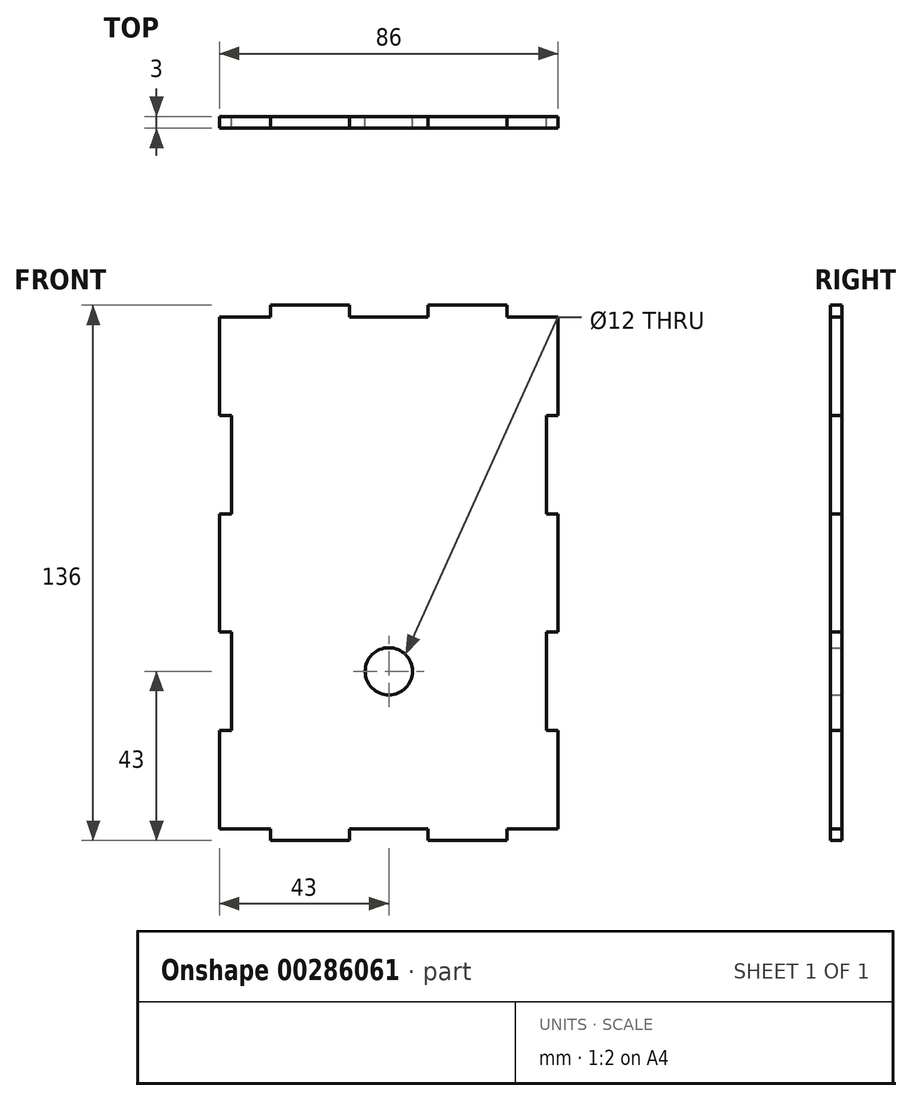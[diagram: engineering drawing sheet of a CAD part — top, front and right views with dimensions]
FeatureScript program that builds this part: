
annotation { "Feature Type Name" : "Feature", "Feature Type Description" : "" }
export const myFeature = defineFeature(function(context is Context, id is Id, definition is map)
    precondition{}
    {
        {
            var Q0;
            Q0=qCreatedBy(makeId("Front.planeOp"),FACE);
            var sketch = newSketch(context, id + "F0", { "sketchPlane" : qUnion([Q0])});
            skLineSegment(sketch, "E0.bottom", {"start": v(40, -65) * mm, "end": v(-40, -65) * mm, "construction": true});
            skLineSegment(sketch, "E0.top", {"start": v(40, 65) * mm, "end": v(-40, 65) * mm, "construction": true});
            skLineSegment(sketch, "E0.left", {"start": v(40, -65) * mm, "end": v(40, 65) * mm, "construction": true});
            skLineSegment(sketch, "E0.right", {"start": v(-40, -65) * mm, "end": v(-40, 65) * mm, "construction": true});
            skPoint(sketch, "E0.middle", {"position": v(0, 0) * mm});
            skLineSegment(sketch, "E1", {"start": v(-40, 65) * mm, "end": v(-43, 65) * mm});
            skLineSegment(sketch, "E2", {"start": v(-43, 65) * mm, "end": v(-43, 40) * mm});
            skLineSegment(sketch, "E3", {"start": v(-43, 40) * mm, "end": v(-40, 40) * mm});
            skLineSegment(sketch, "E4", {"start": v(-40, 40) * mm, "end": v(-40, 15) * mm});
            skLineSegment(sketch, "E5", {"start": v(-40, 15) * mm, "end": v(-43, 15) * mm});
            skLineSegment(sketch, "E6", {"start": v(-43, 15) * mm, "end": v(-43, 0) * mm});
            skLineSegment(sketch, "E7", {"start": v(-40, 65) * mm, "end": v(-30, 65) * mm});
            skLineSegment(sketch, "E8", {"start": v(-30, 65) * mm, "end": v(-30, 68) * mm});
            skLineSegment(sketch, "E9", {"start": v(-30, 68) * mm, "end": v(-10, 68) * mm});
            skLineSegment(sketch, "E10", {"start": v(-10, 68) * mm, "end": v(-10, 65) * mm});
            skLineSegment(sketch, "E11", {"start": v(-10, 65) * mm, "end": v(0, 65) * mm});
            skLineSegment(sketch, "E12.MirrorCS", {"start": v(10, 68) * mm, "end": v(10, 65) * mm});
            skLineSegment(sketch, "E13.MirrorCS", {"start": v(30, 65) * mm, "end": v(30, 68) * mm});
            skLineSegment(sketch, "E14.MirrorCS", {"start": v(40, 15) * mm, "end": v(43, 15) * mm});
            skLineSegment(sketch, "E15.MirrorCS", {"start": v(43, 40) * mm, "end": v(40, 40) * mm});
            skLineSegment(sketch, "E16.MirrorCS", {"start": v(40, 65) * mm, "end": v(43, 65) * mm});
            skLineSegment(sketch, "E17.MirrorCS", {"start": v(30, 68) * mm, "end": v(10, 68) * mm});
            skLineSegment(sketch, "E18.MirrorCS", {"start": v(-40, 65) * mm, "end": v(40, 65) * mm, "construction": true});
            skLineSegment(sketch, "E19.MirrorCS", {"start": v(40, 65) * mm, "end": v(30, 65) * mm});
            skLineSegment(sketch, "E20.MirrorCS", {"start": v(10, 65) * mm, "end": v(0, 65) * mm});
            skLineSegment(sketch, "E21.MirrorCS", {"start": v(43, 15) * mm, "end": v(43, 0) * mm});
            skLineSegment(sketch, "E22.MirrorCS", {"start": v(43, 65) * mm, "end": v(43, 40) * mm});
            skLineSegment(sketch, "E23.MirrorCS", {"start": v(40, 40) * mm, "end": v(40, 15) * mm});
            skLineSegment(sketch, "E24.MirrorCS", {"start": v(30, -65) * mm, "end": v(30, -68) * mm});
            skLineSegment(sketch, "E25.MirrorCS", {"start": v(43, -40) * mm, "end": v(40, -40) * mm});
            skLineSegment(sketch, "E26.MirrorCS", {"start": v(-30, -65) * mm, "end": v(-30, -68) * mm});
            skLineSegment(sketch, "E27.MirrorCS", {"start": v(10, -68) * mm, "end": v(10, -65) * mm});
            skLineSegment(sketch, "E28.MirrorCS", {"start": v(-40, -65) * mm, "end": v(-43, -65) * mm});
            skLineSegment(sketch, "E29.MirrorCS", {"start": v(-43, -40) * mm, "end": v(-40, -40) * mm});
            skLineSegment(sketch, "E30.MirrorCS", {"start": v(40, -15) * mm, "end": v(43, -15) * mm});
            skLineSegment(sketch, "E31.MirrorCS", {"start": v(40, -65) * mm, "end": v(43, -65) * mm});
            skLineSegment(sketch, "E32.MirrorCS", {"start": v(-10, -68) * mm, "end": v(-10, -65) * mm});
            skLineSegment(sketch, "E33.MirrorCS", {"start": v(-40, -15) * mm, "end": v(-43, -15) * mm});
            skLineSegment(sketch, "E34.MirrorCS", {"start": v(40, 65) * mm, "end": v(40, -65) * mm, "construction": true});
            skLineSegment(sketch, "E35.MirrorCS", {"start": v(30, -68) * mm, "end": v(10, -68) * mm});
            skLineSegment(sketch, "E36.MirrorCS", {"start": v(-40, -65) * mm, "end": v(40, -65) * mm, "construction": true});
            skLineSegment(sketch, "E37.MirrorCS", {"start": v(40, -65) * mm, "end": v(30, -65) * mm});
            skLineSegment(sketch, "E38.MirrorCS", {"start": v(43, -15) * mm, "end": v(43, 0) * mm});
            skLineSegment(sketch, "E39.MirrorCS", {"start": v(40, -40) * mm, "end": v(40, -15) * mm});
            skLineSegment(sketch, "E40.MirrorCS", {"start": v(-30, -68) * mm, "end": v(-10, -68) * mm});
            skLineSegment(sketch, "E41.MirrorCS", {"start": v(-40, 65) * mm, "end": v(-40, -65) * mm, "construction": true});
            skLineSegment(sketch, "E42.MirrorCS", {"start": v(-10, -65) * mm, "end": v(0, -65) * mm});
            skLineSegment(sketch, "E43.MirrorCS", {"start": v(-43, -15) * mm, "end": v(-43, 0) * mm});
            skLineSegment(sketch, "E44.MirrorCS", {"start": v(-43, -65) * mm, "end": v(-43, -40) * mm});
            skLineSegment(sketch, "E45.MirrorCS", {"start": v(-40, -40) * mm, "end": v(-40, -15) * mm});
            skLineSegment(sketch, "E46.MirrorCS", {"start": v(-40, -65) * mm, "end": v(-30, -65) * mm});
            skLineSegment(sketch, "E47.MirrorCS", {"start": v(10, -65) * mm, "end": v(0, -65) * mm});
            skLineSegment(sketch, "E48.MirrorCS", {"start": v(43, -65) * mm, "end": v(43, -40) * mm});
            skCircle(sketch, "E49", {"center": v(0, -25) * mm, "radius": 6 * mm});
            skSolve(sketch);
        }
        {
            var Q0;
            Q0=makeQuery(id+"F0.imprint","IMPRINT",FACE,{"disambiguationData":[TD([[makeQuery(id+"F0.imprint","IMPRINT",EDGE,{"derivedFrom":sQuery(id+"F0.wireOp",EDGE,"E1")}),1.0]])]});
            extrude(context, id + "F1", {"entities" : qUnion([Q0]), "depth" : 3 * mm});
        }
    });
